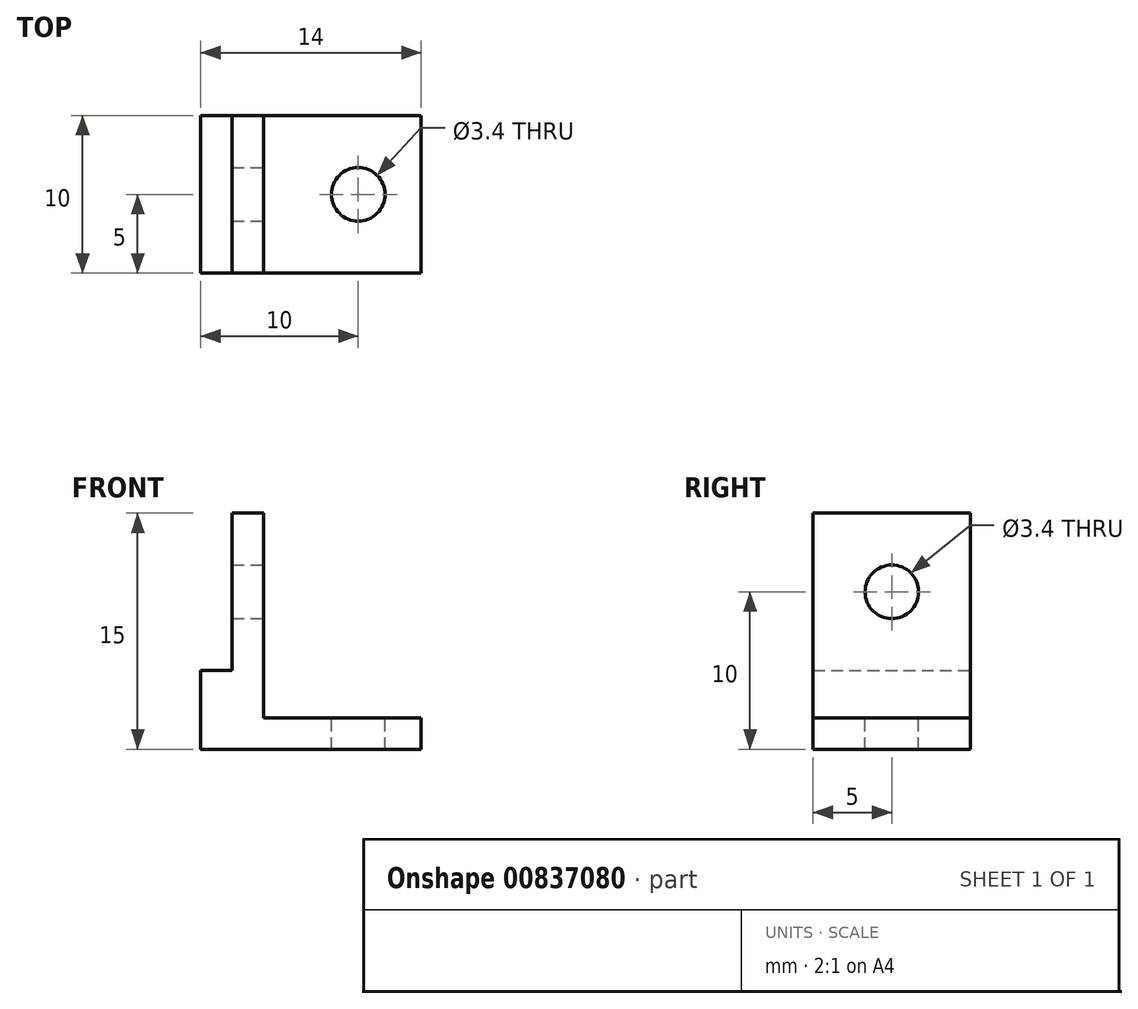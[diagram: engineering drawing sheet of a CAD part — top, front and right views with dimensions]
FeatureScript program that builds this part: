
annotation { "Feature Type Name" : "Feature", "Feature Type Description" : "" }
export const myFeature = defineFeature(function(context is Context, id is Id, definition is map)
    precondition{}
    {
        {
            var Q0;
            Q0=qCreatedBy(makeId("Front.planeOp"),FACE);
            var sketch = newSketch(context, id + "F0", { "sketchPlane" : qUnion([Q0])});
            skLineSegment(sketch, "E0", {"start": v(0, 0) * mm, "end": v(117.98, 0) * mm, "construction": true});
            skLineSegment(sketch, "E1", {"start": v(0, 0) * mm, "end": v(0, 64.98) * mm, "construction": true});
            skLineSegment(sketch, "E2", {"start": v(0, 0) * mm, "end": v(0, 5) * mm});
            skLineSegment(sketch, "E3", {"start": v(0, 5) * mm, "end": v(2, 5) * mm});
            skLineSegment(sketch, "E4", {"start": v(2, 5) * mm, "end": v(2, 15) * mm});
            skLineSegment(sketch, "E5", {"start": v(2, 15) * mm, "end": v(4, 15) * mm});
            skLineSegment(sketch, "E6", {"start": v(4, 15) * mm, "end": v(4, 2) * mm});
            skLineSegment(sketch, "E7", {"start": v(4, 2) * mm, "end": v(14, 2) * mm});
            skLineSegment(sketch, "E8", {"start": v(14, 2) * mm, "end": v(14, 0) * mm});
            skLineSegment(sketch, "E9", {"start": v(14, 0) * mm, "end": v(0, 0) * mm});
            skSolve(sketch);
        }
        {
            var Q0;
            Q0=makeQuery(id+"F0.imprint","IMPRINT",FACE,{"disambiguationData":[TD([[makeQuery(id+"F0.imprint","IMPRINT",EDGE,{"derivedFrom":sQuery(id+"F0.wireOp",EDGE,"E2")}),-1.0]])]});
            extrude(context, id + "F1", {"entities" : qUnion([Q0]), "depth" : 10 * mm, "offsetDistance" : 25 * mm});
        }
        {
            var Q0;
            Q0=makeQuery(id+"F1.opExtrude","SWEPT_FACE",FACE,{"disambiguationData":[OSD([sQuery(id+"F0.wireOp",EDGE,"E6")])]});
            var sketch = newSketch(context, id + "F2", { "sketchPlane" : qUnion([Q0])});
            skLineSegment(sketch, "E10", {"start": v(-10.28, 10) * mm, "end": v(5.82, 10) * mm, "construction": true});
            skLineSegment(sketch, "E11", {"start": v(-5, 24.88) * mm, "end": v(-5, -1.63) * mm, "construction": true});
            skPoint(sketch, "E12", {"position": v(-5, 10) * mm});
            skSolve(sketch);
        }
        {
            var Q0;
            Q0=sQuery(id+"F2.wireOp",VERTEX,"E12");
            var Q1;
            Q1=makeQuery(id+"F1.opExtrude","SWEPT_BODY",BODY,{"disambiguationData":[OSD([sQuery(id+"F0.wireOp",EDGE,"E2"),sQuery(id+"F0.wireOp",EDGE,"E3"),sQuery(id+"F0.wireOp",EDGE,"E4"),sQuery(id+"F0.wireOp",EDGE,"E5"),sQuery(id+"F0.wireOp",EDGE,"E6"),sQuery(id+"F0.wireOp",EDGE,"E7"),sQuery(id+"F0.wireOp",EDGE,"E8"),sQuery(id+"F0.wireOp",EDGE,"E9")])]});
            hole(context, id + "F3", {"style" : HoleStyle.SIMPLE, "endStyle" : HoleEndStyle.THROUGH, "standardTappedOrClearance" : lookupTablePath({ "fit" : "Normal", "standard" : "ISO", "size" : "M3", "type" : "Clearance" }), "standardBlindInLast" : lookupTablePath({ "fit" : "Normal", "standard" : "ISO", "engagement" : "75%", "pitch" : "0.5 mm", "size" : "M3", "type" : "Clearance & tapped" }), "holeDiameter" : 3.4 * mm, "majorDiameter" : 5 * mm, "isTappedThrough" : true, "tappedDepth" : 12 * mm, "tapClearance" : 3, "startFromSketch" : true, "locations" : qUnion([Q0]), "scope" : qUnion([Q1])});
        }
        {
            var Q0;
            Q0=makeQuery(id+"F1.opExtrude","SWEPT_FACE",FACE,{"disambiguationData":[OSD([sQuery(id+"F0.wireOp",EDGE,"E7")])]});
            var sketch = newSketch(context, id + "F4", { "sketchPlane" : qUnion([Q0])});
            skLineSegment(sketch, "E13", {"start": v(26.23, -5) * mm, "end": v(-9.7, -5) * mm});
            skLineSegment(sketch, "E14", {"start": v(10, 4.02) * mm, "end": v(10, -17.95) * mm});
            skPoint(sketch, "E15", {"position": v(10, -5) * mm});
            skSolve(sketch);
        }
        {
            var Q0;
            Q0=sQuery(id+"F4.wireOp",VERTEX,"E15");
            var Q1;
            Q1=makeQuery(id+"F1.opExtrude","SWEPT_BODY",BODY,{"disambiguationData":[OSD([sQuery(id+"F0.wireOp",EDGE,"E2"),sQuery(id+"F0.wireOp",EDGE,"E3"),sQuery(id+"F0.wireOp",EDGE,"E4"),sQuery(id+"F0.wireOp",EDGE,"E5"),sQuery(id+"F0.wireOp",EDGE,"E6"),sQuery(id+"F0.wireOp",EDGE,"E7"),sQuery(id+"F0.wireOp",EDGE,"E8"),sQuery(id+"F0.wireOp",EDGE,"E9")])]});
            hole(context, id + "F5", {"style" : HoleStyle.SIMPLE, "endStyle" : HoleEndStyle.THROUGH, "standardTappedOrClearance" : lookupTablePath({ "fit" : "Normal", "standard" : "ISO", "size" : "M3", "type" : "Clearance" }), "standardBlindInLast" : lookupTablePath({ "fit" : "Normal", "standard" : "ISO", "engagement" : "75%", "pitch" : "0.5 mm", "size" : "M3", "type" : "Clearance & tapped" }), "holeDiameter" : 3.4 * mm, "majorDiameter" : 5 * mm, "isTappedThrough" : true, "tappedDepth" : 12 * mm, "tapClearance" : 3, "startFromSketch" : true, "locations" : qUnion([Q0]), "scope" : qUnion([Q1])});
        }
    });
